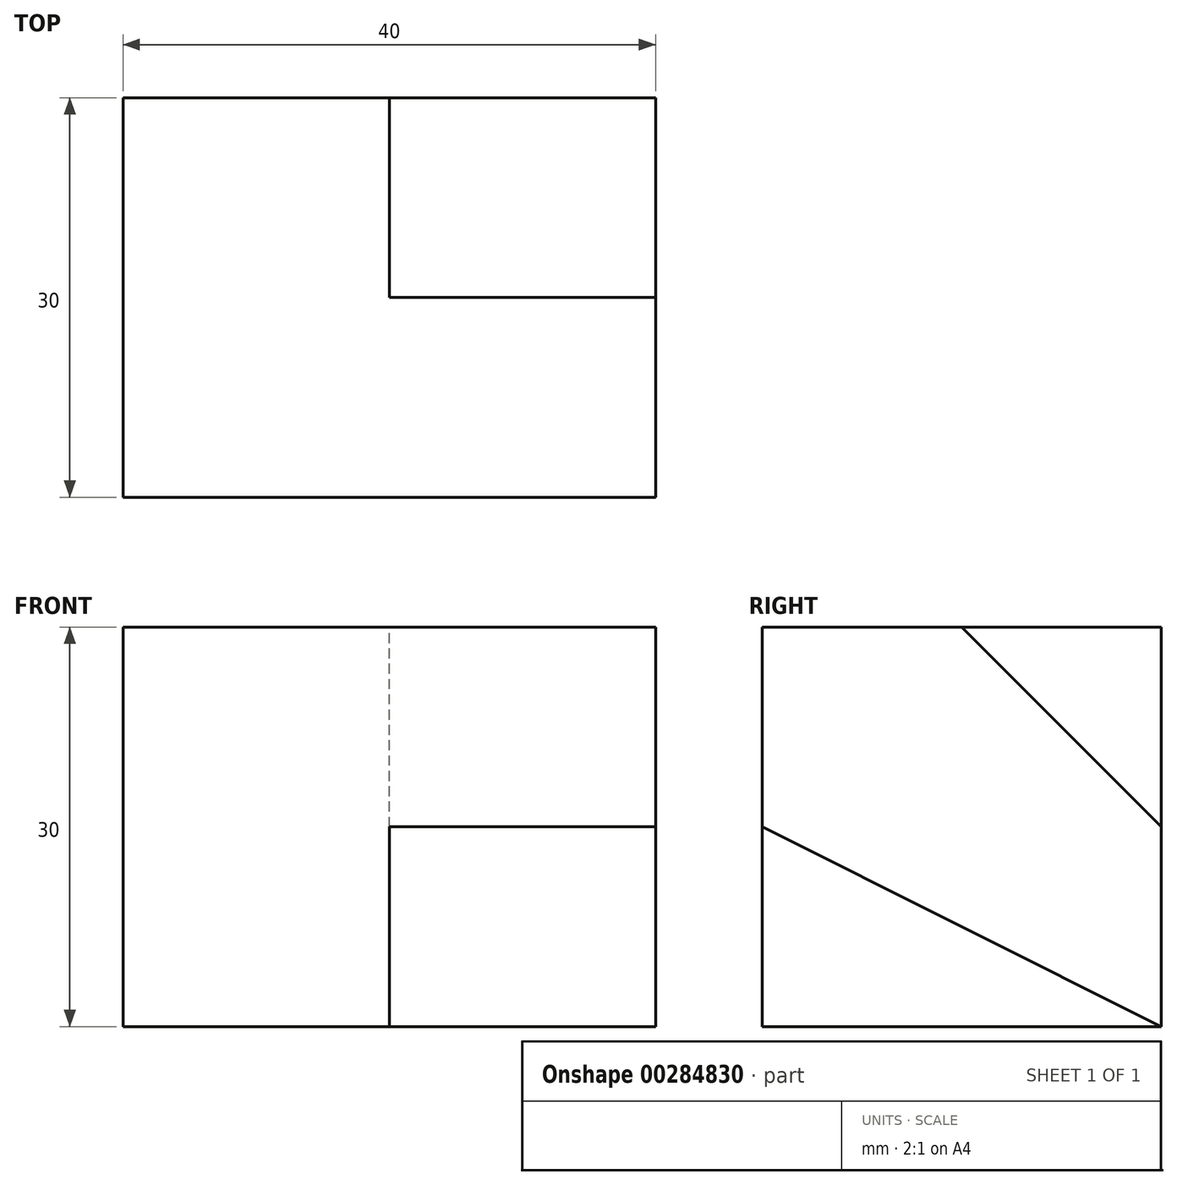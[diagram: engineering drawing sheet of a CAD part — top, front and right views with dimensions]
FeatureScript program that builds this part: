
annotation { "Feature Type Name" : "Feature", "Feature Type Description" : "" }
export const myFeature = defineFeature(function(context is Context, id is Id, definition is map)
    precondition{}
    {
        {
            var Q0;
            Q0=qCreatedBy(makeId("Right.planeOp"),FACE);
            var sketch = newSketch(context, id + "F0", { "sketchPlane" : qUnion([Q0])});
            skLineSegment(sketch, "E0.bottom", {"start": v(0, 0) * mm, "end": v(30, 0) * mm});
            skLineSegment(sketch, "E0.top", {"start": v(0, 30) * mm, "end": v(30, 30) * mm});
            skLineSegment(sketch, "E0.left", {"start": v(0, 0) * mm, "end": v(0, 30) * mm});
            skLineSegment(sketch, "E0.right", {"start": v(30, 0) * mm, "end": v(30, 30) * mm});
            skLineSegment(sketch, "E1", {"start": v(0, 15) * mm, "end": v(30, 15) * mm});
            skLineSegment(sketch, "E2", {"start": v(15, 30) * mm, "end": v(15, 0) * mm});
            skSolve(sketch);
        }
        {
            var Q0;
            Q0=qSketchRegion(id+"F0",true);
            extrude(context, id + "F1", {"entities" : qUnion([Q0]), "depth" : 20 * mm});
        }
        {
            var Q0;
            {var subQ0=sQuery(id+"F0.wireOp",EDGE,"E0.right");var subQ1=sQuery(id+"F0.wireOp",EDGE,"E0.bottom");var subQ2=makeQuery(id+"F0.imprint","INTERSECT",VERTEX,{"derivedFrom":[subQ1,subQ0]});Q0=makeQuery(id+"F0.imprint","IMPRINT",FACE,{"disambiguationData":[TD([[makeQuery(id+"F0.imprint","IMPRINT",EDGE,{"disambiguationData":[TD([[subQ2,1.0]])],"derivedFrom":subQ1}),1.0]])]});}
            var Q1;
            {var subQ0=sQuery(id+"F0.wireOp",EDGE,"E0.right");var subQ1=sQuery(id+"F0.wireOp",EDGE,"E0.top");var subQ2=makeQuery(id+"F0.imprint","INTERSECT",VERTEX,{"derivedFrom":[subQ1,subQ0]});Q1=makeQuery(id+"F0.imprint","IMPRINT",FACE,{"disambiguationData":[TD([[makeQuery(id+"F0.imprint","IMPRINT",EDGE,{"disambiguationData":[TD([[subQ2,1.0]])],"derivedFrom":subQ1}),-1.0]])]});}
            var Q2;
            {var subQ0=sQuery(id+"F0.wireOp",EDGE,"E0.left");var subQ1=sQuery(id+"F0.wireOp",EDGE,"E0.top");var subQ2=makeQuery(id+"F0.imprint","INTERSECT",VERTEX,{"derivedFrom":[subQ1,subQ0]});Q2=makeQuery(id+"F0.imprint","IMPRINT",FACE,{"disambiguationData":[TD([[makeQuery(id+"F0.imprint","IMPRINT",EDGE,{"disambiguationData":[TD([[subQ2,-1.0]])],"derivedFrom":subQ1}),-1.0]])]});}
            extrude(context, id + "F2", {"entities" : qUnion([Q0, Q1, Q2]), "operationType" : NewBodyOperationType.ADD, "depth" : 40 * mm});
        }
        {
            var Q0;
            Q0=makeQuery(id+"F2.opExtrude","CAP_FACE",FACE,{"disambiguationData":[OSD([sQuery(id+"F0.wireOp",EDGE,"E0.bottom"),sQuery(id+"F0.wireOp",EDGE,"E0.top"),sQuery(id+"F0.wireOp",EDGE,"E0.left"),sQuery(id+"F0.wireOp",EDGE,"E0.right"),sQuery(id+"F0.wireOp",EDGE,"E1"),sQuery(id+"F0.wireOp",EDGE,"E2")])],"isStart":false});
            var sketch = newSketch(context, id + "F3", { "sketchPlane" : qUnion([Q0])});
            skLineSegment(sketch, "E3", {"start": v(15, 30) * mm, "end": v(30, 15) * mm});
            skSolve(sketch);
        }
        {
            var Q0;
            {var subQ0=sQuery(id+"F3.wireOp",EDGE,"E3");Q0=makeQuery(id+"F3.imprint","IMPRINT",FACE,{"disambiguationData":[TD([[makeQuery(id+"F3.imprint","IMPRINT",EDGE,{"derivedFrom":subQ0}),1.0]])]});}
            extrude(context, id + "F4", {"entities" : qUnion([Q0]), "operationType" : NewBodyOperationType.REMOVE, "oppositeDirection" : true, "depth" : 20 * mm});
        }
        {
            var Q0;
            Q0=makeQuery(id+"F1.opExtrude","CAP_FACE",FACE,{"disambiguationData":[OSD([sQuery(id+"F0.wireOp",EDGE,"E0.bottom"),sQuery(id+"F0.wireOp",EDGE,"E0.top"),sQuery(id+"F0.wireOp",EDGE,"E0.left"),sQuery(id+"F0.wireOp",EDGE,"E0.right")])],"isStart":false});
            var sketch = newSketch(context, id + "F5", { "sketchPlane" : qUnion([Q0])});
            skLineSegment(sketch, "E4", {"start": v(0, 15) * mm, "end": v(15, 0) * mm});
            skSolve(sketch);
        }
        {
            var Q0;
            Q0=makeQuery(id+"F5.imprint","IMPRINT",FACE,{"disambiguationData":[TD([[makeQuery(id+"F5.imprint","IMPRINT",EDGE,{"derivedFrom":sQuery(id+"F5.wireOp",EDGE,"E4")}),1.0]])]});
            extrude(context, id + "F6", {"entities" : qUnion([Q0]), "operationType" : NewBodyOperationType.ADD, "depth" : 20 * mm});
        }
        {
            var Q0;
            {var subQ0=sQuery(id+"F0.wireOp",EDGE,"E2");var subQ1=sQuery(id+"F0.wireOp",EDGE,"E1");var subQ2=sQuery(id+"F0.wireOp",EDGE,"E0.right");var subQ3=sQuery(id+"F0.wireOp",EDGE,"E0.left");var subQ4=sQuery(id+"F0.wireOp",EDGE,"E0.top");var subQ5=sQuery(id+"F0.wireOp",EDGE,"E0.bottom");Q0=makeQuery(id+"F6.boolean.opBoolean","MERGE",FACE,{"derivedFrom":[makeQuery(id+"F2.opExtrude","CAP_FACE",FACE,{"disambiguationData":[OSD([subQ5,subQ4,subQ3,subQ2,subQ1,subQ0])],"isStart":false}),makeQuery(id+"F6.opExtrude","CAP_FACE",FACE,{"disambiguationData":[OSD([subQ5,subQ4,subQ3,subQ2,subQ1,subQ0,sQuery(id+"F5.wireOp",EDGE,"E4")])],"isStart":false})]});}
            var sketch = newSketch(context, id + "F7", { "sketchPlane" : qUnion([Q0])});
            skLineSegment(sketch, "E5", {"start": v(0, 15) * mm, "end": v(30, 0) * mm});
            skSolve(sketch);
        }
        {
            var Q0;
            Q0=makeQuery(id+"F7.imprint","IMPRINT",FACE,{"disambiguationData":[TD([[makeQuery(id+"F7.imprint","IMPRINT",EDGE,{"derivedFrom":sQuery(id+"F7.wireOp",EDGE,"E5")}),-1.0]])]});
            extrude(context, id + "F8", {"entities" : qUnion([Q0]), "operationType" : NewBodyOperationType.REMOVE, "oppositeDirection" : true, "depth" : 20 * mm});
        }
    });
